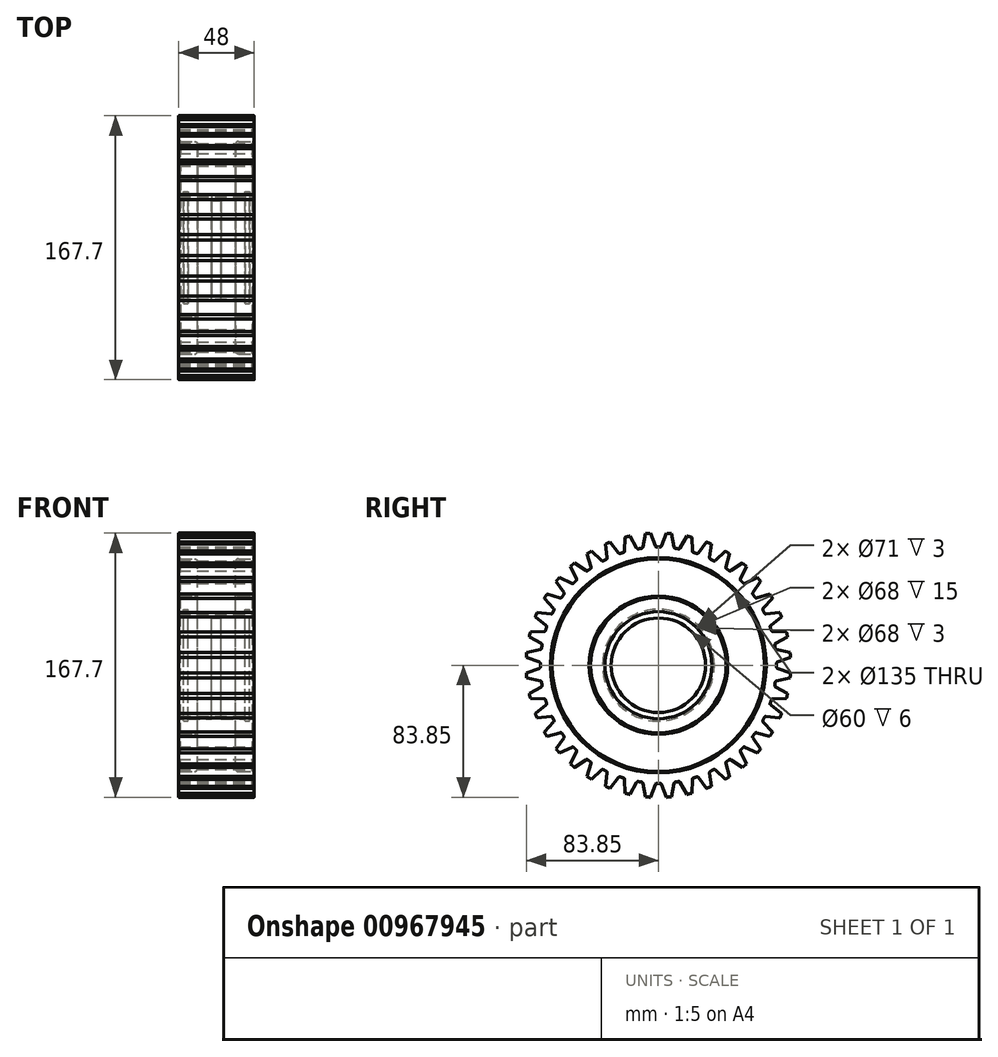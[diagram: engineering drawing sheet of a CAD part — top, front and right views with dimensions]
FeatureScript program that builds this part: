
annotation { "Feature Type Name" : "Feature", "Feature Type Description" : "" }
export const myFeature = defineFeature(function(context is Context, id is Id, definition is map)
    precondition{}
    {
        {
            var Q0;
            Q0=qCreatedBy(makeId("Front.planeOp"),FACE);
            var sketch = newSketch(context, id + "F0", { "sketchPlane" : qUnion([Q0])});
            skLineSegment(sketch, "E0.bottom", {"start": v(0, 0) * mm, "end": v(-24, 0) * mm, "construction": true});
            skLineSegment(sketch, "E0.top", {"start": v(0, 84) * mm, "end": v(-24, 84) * mm});
            skLineSegment(sketch, "E0.left", {"start": v(0, 0) * mm, "end": v(0, 84) * mm, "construction": true});
            skLineSegment(sketch, "E0.right", {"start": v(-24, 34) * mm, "end": v(-24, 44) * mm});
            skLineSegment(sketch, "E1", {"start": v(-24, 34) * mm, "end": v(-21, 34) * mm});
            skLineSegment(sketch, "E2", {"start": v(-21, 34) * mm, "end": v(-21, 35.5) * mm});
            skLineSegment(sketch, "E3", {"start": v(-21, 35.5) * mm, "end": v(-18, 35.5) * mm});
            skLineSegment(sketch, "E4", {"start": v(-18, 35.5) * mm, "end": v(-18, 34) * mm});
            skLineSegment(sketch, "E5", {"start": v(-18, 34) * mm, "end": v(-3, 34) * mm});
            skLineSegment(sketch, "E6", {"start": v(-3, 34) * mm, "end": v(-3, 30) * mm});
            skLineSegment(sketch, "E7", {"start": v(-3, 30) * mm, "end": v(0, 30) * mm});
            skLineSegment(sketch, "E8", {"start": v(-24, 44) * mm, "end": v(-14, 44) * mm});
            skLineSegment(sketch, "E9", {"start": v(-12, 46) * mm, "end": v(-12, 65.5) * mm});
            skLineSegment(sketch, "E10", {"start": v(-14, 67.5) * mm, "end": v(-24, 67.5) * mm});
            skLineSegment(sketch, "E11.trimOffspring", {"start": v(-24, 67.5) * mm, "end": v(-24, 84) * mm});
            skPoint(sketch, "E12.visualSharp", {"position": v(-12, 67.5) * mm});
            skArc(sketch, "E12.filletArc", {"start": v(-12, 65.5) * mm, "mid": v(-12.59, 66.91) * mm, "end": v(-14, 67.5) * mm});
            skPoint(sketch, "E13.visualSharp", {"position": v(-12, 44) * mm});
            skArc(sketch, "E13.filletArc", {"start": v(-14, 44) * mm, "mid": v(-12.59, 44.59) * mm, "end": v(-12, 46) * mm});
            skLineSegment(sketch, "E14.MirrorCS", {"start": v(0, 84) * mm, "end": v(24, 84) * mm});
            skLineSegment(sketch, "E15.MirrorCS", {"start": v(24, 67.5) * mm, "end": v(24, 84) * mm});
            skLineSegment(sketch, "E16.MirrorCS", {"start": v(14, 67.5) * mm, "end": v(24, 67.5) * mm});
            skLineSegment(sketch, "E17.MirrorCS", {"start": v(12, 46) * mm, "end": v(12, 65.5) * mm});
            skLineSegment(sketch, "E18.MirrorCS", {"start": v(24, 44) * mm, "end": v(14, 44) * mm});
            skLineSegment(sketch, "E19.MirrorCS", {"start": v(24, 34) * mm, "end": v(24, 44) * mm});
            skLineSegment(sketch, "E20.MirrorCS", {"start": v(18, 34) * mm, "end": v(3, 34) * mm});
            skLineSegment(sketch, "E21.MirrorCS", {"start": v(21, 34) * mm, "end": v(21, 35.5) * mm});
            skLineSegment(sketch, "E22.MirrorCS", {"start": v(18, 35.5) * mm, "end": v(18, 34) * mm});
            skLineSegment(sketch, "E23.MirrorCS", {"start": v(21, 35.5) * mm, "end": v(18, 35.5) * mm});
            skLineSegment(sketch, "E24.MirrorCS", {"start": v(3, 34) * mm, "end": v(3, 30) * mm});
            skLineSegment(sketch, "E25.MirrorCS", {"start": v(3, 30) * mm, "end": v(0, 30) * mm});
            skLineSegment(sketch, "E26.MirrorCS", {"start": v(24, 34) * mm, "end": v(21, 34) * mm});
            skArc(sketch, "E27.MirrorCS", {"start": v(14, 44) * mm, "mid": v(12.59, 44.59) * mm, "end": v(12, 46) * mm});
            skArc(sketch, "E28.MirrorCS", {"start": v(12, 65.5) * mm, "mid": v(12.59, 66.91) * mm, "end": v(14, 67.5) * mm});
            skSolve(sketch);
        }
        {
            var Q0;
            Q0=makeQuery(id+"F0.imprint","IMPRINT",FACE,{"disambiguationData":[TD([[makeQuery(id+"F0.imprint","IMPRINT",EDGE,{"derivedFrom":sQuery(id+"F0.wireOp",EDGE,"E0.top")}),1.0]])]});
            var Q1;
            Q1=sQuery(id+"F0.wireOp",EDGE,"E0.bottom");
            revolve(context, id + "F1", {"surfaceOperationType" : NewSurfaceOperationType.NEW, "entities" : qUnion([Q0]), "axis" : qUnion([Q1]), "revolveType" : RevolveType.FULL});
        }
        {
            var Q0;
            Q0=qCreatedBy(makeId("Right.planeOp"),FACE);
            var sketch = newSketch(context, id + "F2", { "sketchPlane" : qUnion([Q0])});
            skArc(sketch, "E29", {"start": v(1.04, 75) * mm, "mid": v(0, 75) * mm, "end": v(-1.04, 75) * mm});
            skLineSegment(sketch, "E30", {"start": v(0, 0) * mm, "end": v(0, 84) * mm, "construction": true});
            skLineSegment(sketch, "E31", {"start": v(2, 75.65) * mm, "end": v(4.98, 83.85) * mm});
            skLineSegment(sketch, "E32.MirrorCS", {"start": v(-2, 75.65) * mm, "end": v(-4.98, 83.85) * mm});
            skArc(sketch, "E33.0", {"start": v(4.98, 83.85) * mm, "mid": v(0, 84) * mm, "end": v(-4.98, 83.85) * mm});
            skPoint(sketch, "E34.visualSharp", {"position": v(-1.75, 74.98) * mm});
            skArc(sketch, "E34.filletArc", {"start": v(-2, 75.65) * mm, "mid": v(-1.62, 75.17) * mm, "end": v(-1.04, 75) * mm});
            skPoint(sketch, "E35.visualSharp", {"position": v(1.75, 74.98) * mm});
            skArc(sketch, "E35.filletArc", {"start": v(1.04, 75) * mm, "mid": v(1.62, 75.17) * mm, "end": v(2, 75.65) * mm});
            skSolve(sketch);
        }
        {
            var Q0;
            Q0 = qSketchRegion(id + "F2", true);
            extrude(context, id + "F3", {"entities" : qUnion([Q0]), "operationType" : NewBodyOperationType.REMOVE, "endBound" : BoundingType.SYMMETRIC, "oppositeDirection" : true, "depth" : 50 * mm, "offsetDistance" : 25 * mm});
        }
        {
            var Q0;
            Q0=makeQuery(id+"F3.boolean.opBoolean","COPY",FACE,{"derivedFrom":makeQuery(id+"F3.opExtrude","SWEPT_FACE",FACE,{"disambiguationData":[OSD([sQuery(id+"F2.wireOp",EDGE,"E32.MirrorCS")])]})});
            var Q1;
            Q1=makeQuery(id+"F3.boolean.opBoolean","COPY",FACE,{"derivedFrom":makeQuery(id+"F3.opExtrude","SWEPT_FACE",FACE,{"disambiguationData":[OSD([sQuery(id+"F2.wireOp",EDGE,"E34.filletArc")])]})});
            var Q2;
            Q2=makeQuery(id+"F3.boolean.opBoolean","COPY",FACE,{"derivedFrom":makeQuery(id+"F3.opExtrude","SWEPT_FACE",FACE,{"disambiguationData":[OSD([sQuery(id+"F2.wireOp",EDGE,"E29")])]})});
            var Q3;
            Q3=makeQuery(id+"F3.boolean.opBoolean","COPY",FACE,{"derivedFrom":makeQuery(id+"F3.opExtrude","SWEPT_FACE",FACE,{"disambiguationData":[OSD([sQuery(id+"F2.wireOp",EDGE,"E35.filletArc")])]})});
            var Q4;
            Q4=makeQuery(id+"F3.boolean.opBoolean","COPY",FACE,{"derivedFrom":makeQuery(id+"F3.opExtrude","SWEPT_FACE",FACE,{"disambiguationData":[OSD([sQuery(id+"F2.wireOp",EDGE,"E31")])]})});
            var Q5;
            Q5=makeQuery(id+"F1.opRevolve","SWEPT_FACE",FACE,{"disambiguationData":[OSD([sQuery(id+"F0.wireOp",EDGE,"E0.top"),sQuery(id+"F0.wireOp",EDGE,"E14.MirrorCS")])]});
            circularPattern(context, id + "F4", {"patternType" : PatternType.FACE, "faces" : qUnion([Q0, Q1, Q2, Q3, Q4]), "axis" : qUnion([Q5]), "angle" : 9 * degree, "instanceCount" : 40, "oppositeDirection" : true});
        }
        {
            var Q0;
            Q0=makeQuery(id+"F1.opRevolve","SWEPT_EDGE",EDGE,{"disambiguationData":[OSD([sQuery(id+"F0.wireOp",EDGE,"E15.MirrorCS"),sQuery(id+"F0.wireOp",EDGE,"E16.MirrorCS")])]});
            var Q1;
            Q1=makeQuery(id+"F1.opRevolve","SWEPT_EDGE",EDGE,{"disambiguationData":[OSD([sQuery(id+"F0.wireOp",EDGE,"E18.MirrorCS"),sQuery(id+"F0.wireOp",EDGE,"E19.MirrorCS")])]});
            var Q2;
            Q2=makeQuery(id+"F1.opRevolve","SWEPT_EDGE",EDGE,{"disambiguationData":[OSD([sQuery(id+"F0.wireOp",EDGE,"E10"),sQuery(id+"F0.wireOp",EDGE,"E11.trimOffspring")])]});
            var Q3;
            Q3=makeQuery(id+"F1.opRevolve","SWEPT_EDGE",EDGE,{"disambiguationData":[OSD([sQuery(id+"F0.wireOp",EDGE,"E0.right"),sQuery(id+"F0.wireOp",EDGE,"E8")])]});
            chamfer(context, id + "F5", {"entities" : qUnion([Q0, Q1, Q2, Q3]), "chamferType" : ChamferType.OFFSET_ANGLE, "width" : 1 * mm, "oppositeDirection" : false, "angle" : 45 * degree, "tangentPropagation" : true});
        }
    });
